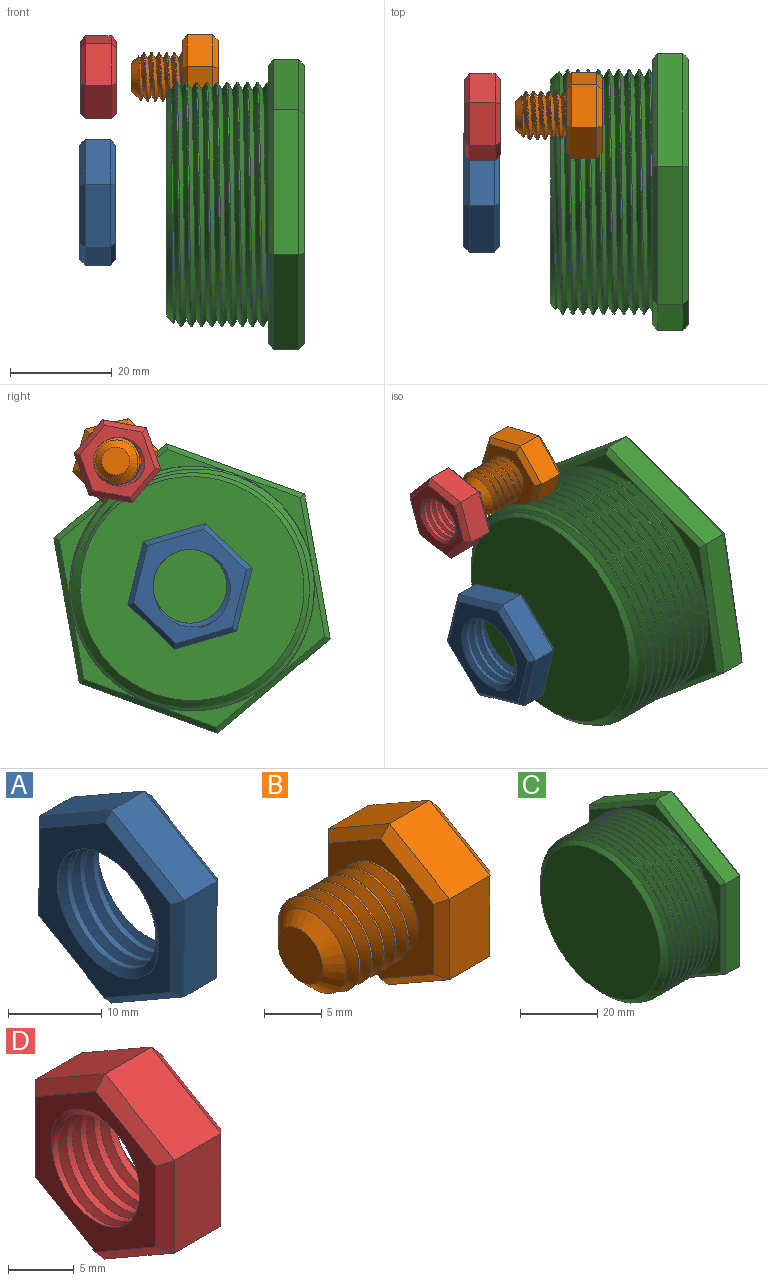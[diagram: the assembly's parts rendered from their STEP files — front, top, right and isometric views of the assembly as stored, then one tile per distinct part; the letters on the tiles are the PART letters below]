
ASSEMBLY  parts=4 mates=2
PART A: 23 faces, bbox 9.3x22.7x26 mm
  f0: cylinder r=7.24mm len=14.48mm, axis (1,0,0), area 111.6mm2, adj f7,f8,f21,f22
  f1: plane 10.98x6.38mm, normal (0,-0.5,0.86), area 63.5mm2, adj f2,f6,f14,f18
  f2: plane 12.7x5mm, normal (0,-1,0), area 63.5mm2, adj f1,f3,f12,f16
  f3: plane 11.02x6.32mm, normal (0,-0.5,-0.87), area 63.5mm2, adj f2,f4,f10,f15
  f4: plane 10.98x6.38mm, normal (0,0.5,-0.86), area 63.5mm2, adj f3,f5,f9,f17
  f5: plane 12.7x5mm, normal (0,1,0), area 63.5mm2, adj f4,f6,f11,f19
  f6: plane 11.02x6.32mm, normal (0,0.5,0.87), area 63.5mm2, adj f1,f5,f13,f20
  f7: plane 23.73x20.67mm, normal (-1,0,0), area 164.4mm2, adj f0,f9,f10,f11,f12,f13,f14,f21
  f8: plane 23.73x20.67mm, normal (1,0,0), area 164.4mm2, adj f0,f15,f16,f17,f18,f19,f20,f21
  f9: plane 10.99x6.96mm, normal (-0.71,0.36,-0.61), area 17.1mm2, adj f4,f7,f10,f11
  f10: plane 11.02x6.9mm, normal (-0.71,-0.35,-0.61), area 17.1mm2, adj f3,f7,f9,f12
  f11: plane 12.7x1.03mm, normal (-0.71,0.71,0), area 17.1mm2, adj f5,f7,f9,f13
  f12: plane 12.7x1.03mm, normal (-0.71,-0.71,0), area 17.1mm2, adj f2,f7,f10,f14
  f13: plane 11.02x6.9mm, normal (-0.71,0.35,0.61), area 17.1mm2, adj f6,f7,f11,f14
  f14: plane 10.99x6.96mm, normal (-0.71,-0.36,0.61), area 17.1mm2, adj f1,f7,f12,f13
  f15: plane 11.02x6.9mm, normal (0.71,-0.35,-0.61), area 17.1mm2, adj f3,f8,f16,f17
  f16: plane 12.7x1.03mm, normal (0.71,-0.71,0), area 17.1mm2, adj f2,f8,f15,f18
  f17: plane 10.99x6.96mm, normal (0.71,0.36,-0.61), area 17.1mm2, adj f4,f8,f15,f19
  f18: plane 10.99x6.96mm, normal (0.71,-0.36,0.61), area 17.1mm2, adj f1,f8,f16,f20
  f19: plane 12.7x1.03mm, normal (0.71,0.71,0), area 17.1mm2, adj f5,f8,f17,f20
  f20: plane 11.02x6.9mm, normal (0.71,0.35,0.61), area 17.1mm2, adj f6,f8,f18,f19
  f21: bspline ~19.31x16.73mm, area 223mm2, adj f0,f7,f8,f22
  f22: bspline ~19.31x16.73mm, area 223mm2, adj f0,f7,f8,f21
PART B: 25 faces, bbox 17.8x15.9x18.1 mm
  f0: cylinder r=4.75mm len=9.5mm, axis (1,0,0), area 28.1mm2, adj f1,f2,f4,f12
  f1: bspline ~10.97x9.91mm, area 196.7mm2, adj f0,f2,f4,f12
  f2: bspline ~10.97x10.66mm, area 196.6mm2, adj f0,f1,f4,f12
  f3: plane 5.5x5.5mm, normal (-1,0,0), area 23.8mm2, adj f4
  f4: cone r=4.75mm half-angle=45deg, axis (1,0,0), area 47.4mm2, adj f0,f1,f2,f3
  f5: plane 7.48x5mm, normal (0,-0.5,0.86), area 43.3mm2, adj f6,f10,f18,f22
  f6: plane 8.66x5mm, normal (0,-1,0), area 43.3mm2, adj f5,f7,f16,f20
  f7: plane 7.52x5mm, normal (0,-0.5,-0.87), area 43.3mm2, adj f6,f8,f14,f19
  f8: plane 7.48x5mm, normal (0,0.5,-0.86), area 43.3mm2, adj f7,f9,f13,f21
  f9: plane 8.66x5mm, normal (0,1,0), area 43.3mm2, adj f8,f10,f15,f23
  f10: plane 7.52x5mm, normal (0,0.5,0.87), area 43.3mm2, adj f5,f9,f17,f24
  f11: plane 15.01x13.03mm, normal (1,0,0), area 146.4mm2, adj f13,f14,f15,f16,f17,f18
  f12: plane 15.83x13.85mm, normal (-1,0,0), area 89.2mm2, adj f0,f1,f2,f19,f20,f21,f22,f23
  f13: plane 7.49x4.93mm, normal (0.71,0.36,-0.61), area 11.4mm2, adj f8,f11,f14,f15
  f14: plane 7.52x4.88mm, normal (0.71,-0.35,-0.61), area 11.4mm2, adj f7,f11,f13,f16
  f15: plane 8.66x1.03mm, normal (0.71,0.71,0), area 11.4mm2, adj f9,f11,f13,f17
  f16: plane 8.66x1.03mm, normal (0.71,-0.71,0), area 11.4mm2, adj f6,f11,f14,f18
  f17: plane 7.52x4.88mm, normal (0.71,0.35,0.61), area 11.4mm2, adj f10,f11,f15,f18
  f18: plane 7.49x4.93mm, normal (0.71,-0.36,0.61), area 11.4mm2, adj f5,f11,f16,f17
  f19: plane 7.52x4.88mm, normal (-0.71,-0.35,-0.61), area 11.4mm2, adj f7,f12,f20,f21
  f20: plane 8.66x1.03mm, normal (-0.71,-0.71,0), area 11.4mm2, adj f6,f12,f19,f22
  f21: plane 7.49x4.93mm, normal (-0.71,0.36,-0.61), area 11.4mm2, adj f8,f12,f19,f23
  f22: plane 7.49x4.93mm, normal (-0.71,-0.36,0.61), area 11.4mm2, adj f5,f12,f20,f24
  f23: plane 8.66x1.03mm, normal (-0.71,0.71,0), area 11.4mm2, adj f9,f12,f21,f24
  f24: plane 7.52x4.88mm, normal (-0.71,0.35,0.61), area 11.4mm2, adj f10,f12,f22,f23
PART C: 26 faces, bbox 28.7x56.5x58.8 mm
  f0: cylinder r=24mm len=48mm, axis (1,0,0), area 434.6mm2, adj f1,f2,f5,f13
  f1: bspline ~55.43x48mm, area 2398.3mm2, adj f0,f2,f4,f5,f13
  f2: bspline ~55.43x48mm, area 2402.1mm2, adj f0,f1,f4,f5,f13
  f3: plane 44x44mm, normal (-1,0,0), area 1520.5mm2, adj f4
  f4: cone r=24mm half-angle=45deg, axis (1,0,0), area 226.8mm2, adj f1,f2,f3,f5
  f5: cone r=24mm half-angle=45deg, axis (1,0,0), area 43.3mm2, adj f0,f1,f2,f4
  f6: plane 24.98x14.47mm, normal (0,-0.5,0.87), area 144.3mm2, adj f7,f11,f19,f23
  f7: plane 28.87x5mm, normal (0,-1,0), area 144.3mm2, adj f6,f8,f17,f21
  f8: plane 25.02x14.4mm, normal (0,-0.5,-0.87), area 144.3mm2, adj f7,f9,f15,f20
  f9: plane 24.98x14.47mm, normal (0,0.5,-0.87), area 144.3mm2, adj f8,f10,f14,f22
  f10: plane 28.87x5mm, normal (0,1,0), area 144.3mm2, adj f9,f11,f16,f24
  f11: plane 25.02x14.4mm, normal (0,0.5,0.87), area 144.3mm2, adj f6,f10,f18,f25
  f12: plane 55.43x48.04mm, normal (1,0,0), area 1995.3mm2, adj f14,f15,f16,f17,f18,f19
  f13: plane 56.46x49.08mm, normal (-1,0,0), area 283.6mm2, adj f0,f1,f2,f20,f21,f22,f23,f24
  f14: plane 24.98x15.05mm, normal (0.71,0.35,-0.61), area 40mm2, adj f9,f12,f15,f16
  f15: plane 25.02x14.98mm, normal (0.71,-0.35,-0.61), area 40mm2, adj f8,f12,f14,f17
  f16: plane 28.87x1.04mm, normal (0.71,0.71,0), area 40mm2, adj f10,f12,f14,f18
  f17: plane 28.87x1.04mm, normal (0.71,-0.71,0), area 40mm2, adj f7,f12,f15,f19
  f18: plane 25.02x14.98mm, normal (0.71,0.35,0.61), area 40mm2, adj f11,f12,f16,f19
  f19: plane 24.98x15.05mm, normal (0.71,-0.35,0.61), area 40mm2, adj f6,f12,f17,f18
  f20: plane 25.02x14.98mm, normal (-0.71,-0.35,-0.61), area 40mm2, adj f8,f13,f21,f22
  f21: plane 28.87x1.04mm, normal (-0.71,-0.71,0), area 40mm2, adj f7,f13,f20,f23
  f22: plane 24.98x15.05mm, normal (-0.71,0.35,-0.61), area 40mm2, adj f9,f13,f20,f24
  f23: plane 24.98x15.05mm, normal (-0.71,-0.35,0.61), area 40mm2, adj f6,f13,f21,f25
  f24: plane 28.87x1.04mm, normal (-0.71,0.71,0), area 40mm2, adj f10,f13,f22,f25
  f25: plane 25.02x14.98mm, normal (-0.71,0.35,0.61), area 40mm2, adj f11,f13,f23,f24
PART D: 23 faces, bbox 9.1x15.4x17.7 mm
  f0: plane 7.49x5mm, normal (0,-0.5,0.86), area 43.3mm2, adj f1,f5,f13,f17
  f1: plane 8.66x5mm, normal (0,-1,0), area 43.3mm2, adj f0,f2,f11,f15
  f2: plane 7.51x5mm, normal (0,-0.5,-0.87), area 43.3mm2, adj f1,f3,f9,f14
  f3: plane 7.49x5mm, normal (0,0.5,-0.86), area 43.3mm2, adj f2,f4,f8,f16
  f4: plane 8.66x5mm, normal (0,1,0), area 43.3mm2, adj f3,f5,f10,f18
  f5: plane 7.51x5mm, normal (0,0.5,0.87), area 43.3mm2, adj f0,f4,f12,f19
  f6: plane 15.37x13.38mm, normal (-1,0,0), area 71.4mm2, adj f8,f9,f10,f11,f12,f13,f20,f21
  f7: plane 15.37x13.38mm, normal (1,0,0), area 71.4mm2, adj f14,f15,f16,f17,f18,f19,f20,f21
  f8: plane 7.49x4.93mm, normal (-0.71,0.36,-0.61), area 11.4mm2, adj f3,f6,f9,f10
  f9: plane 7.51x4.89mm, normal (-0.71,-0.35,-0.61), area 11.4mm2, adj f2,f6,f8,f11
  f10: plane 8.66x1.02mm, normal (-0.71,0.71,0), area 11.4mm2, adj f4,f6,f8,f12
  f11: plane 8.66x1.02mm, normal (-0.71,-0.71,0), area 11.4mm2, adj f1,f6,f9,f13
  f12: plane 7.51x4.89mm, normal (-0.71,0.35,0.61), area 11.4mm2, adj f5,f6,f10,f13
  f13: plane 7.49x4.93mm, normal (-0.71,-0.36,0.61), area 11.4mm2, adj f0,f6,f11,f12
  f14: plane 7.51x4.89mm, normal (0.71,-0.35,-0.61), area 11.4mm2, adj f2,f7,f15,f16
  f15: plane 8.66x1.02mm, normal (0.71,-0.71,0), area 11.4mm2, adj f1,f7,f14,f17
  f16: plane 7.49x4.93mm, normal (0.71,0.36,-0.61), area 11.4mm2, adj f3,f7,f14,f18
  f17: plane 7.49x4.93mm, normal (0.71,-0.36,0.61), area 11.4mm2, adj f0,f7,f15,f19
  f18: plane 8.66x1.02mm, normal (0.71,0.71,0), area 11.4mm2, adj f4,f7,f16,f19
  f19: plane 7.51x4.89mm, normal (0.71,0.35,0.61), area 11.4mm2, adj f5,f7,f17,f18
  f20: cylinder r=4.66mm len=9.32mm, axis (1,0,0), area 85.4mm2, adj f6,f7,f21,f22
  f21: bspline ~12.5x10.82mm, area 128.4mm2, adj f6,f7,f20,f22
  f22: bspline ~12.5x10.82mm, area 128.5mm2, adj f6,f7,f20,f21
PLACE A rot(axis=(0,0.6,-0.8),180deg) t=(-55.27,-6.86,23.48)mm fixed
PLACE B rot(axis=(-1,0,0),43.8deg) t=(-31.66,7.73,48.08)mm
PLACE C rot(axis=(1,0,0),109.9deg) t=(-14.77,-7.25,23.06)mm
PLACE D rot(axis=(1,0,0),100.2deg) t=(-48.16,7.38,48.02)mm fixed
MATE cylindrical C.f0 <-> A.f7  axis (-1,0,0) through (-38.27,-7.25,23.06)mm
MATE cylindrical B.f0 <-> D.f6  axis (-1,0,0) through (-45.16,7.73,48.08)mm
